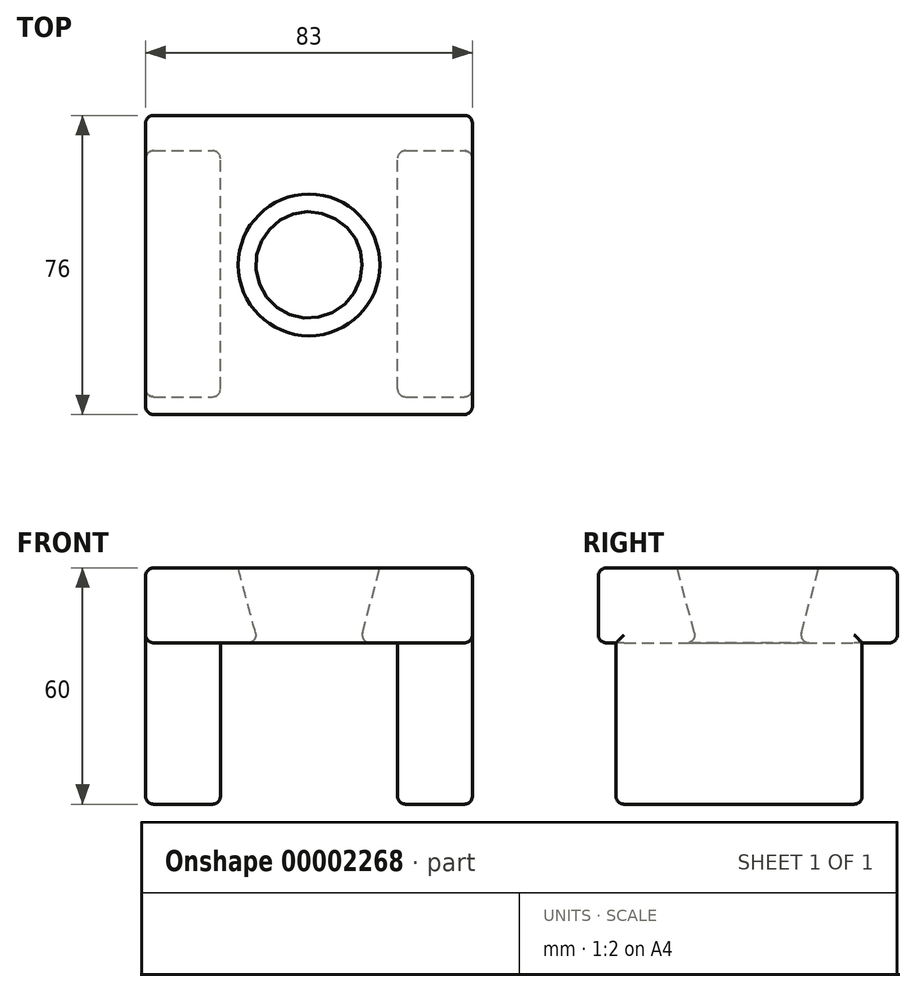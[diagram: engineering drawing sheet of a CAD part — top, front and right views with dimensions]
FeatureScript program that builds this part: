
annotation { "Feature Type Name" : "Feature", "Feature Type Description" : "" }
export const myFeature = defineFeature(function(context is Context, id is Id, definition is map)
    precondition{}
    {
        {
            var Q0;
            Q0=qCreatedBy(makeId("Top.planeOp"),FACE);
            var sketch = newSketch(context, id + "F0", { "sketchPlane" : qUnion([Q0])});
            skCircle(sketch, "E0", {"center": v(0, 0) * mm, "radius": 18 * mm});
            skLineSegment(sketch, "E1.bottom", {"start": v(41.5, 38) * mm, "end": v(-41.5, 38) * mm});
            skLineSegment(sketch, "E1.top", {"start": v(41.5, -38) * mm, "end": v(-41.5, -38) * mm});
            skLineSegment(sketch, "E1.left", {"start": v(41.5, 38) * mm, "end": v(41.5, -38) * mm});
            skLineSegment(sketch, "E1.right", {"start": v(-41.5, 38) * mm, "end": v(-41.5, -38) * mm});
            skSolve(sketch);
        }
        {
            var Q0;
            Q0=makeQuery(id+"F0.imprint","IMPRINT",FACE,{"disambiguationData":[TD([[makeQuery(id+"F0.imprint","IMPRINT",EDGE,{"derivedFrom":sQuery(id+"F0.wireOp",EDGE,"E0")}),-1.0]])]});
            var Q1;
            Q1=makeQuery(id+"F0.imprint","IMPRINT",FACE,{"disambiguationData":[TD([[makeQuery(id+"F0.imprint","IMPRINT",EDGE,{"derivedFrom":sQuery(id+"F0.wireOp",EDGE,"E0")}),1.0]])]});
            extrude(context, id + "F1", {"entities" : qUnion([Q0, Q1]), "oppositeDirection" : true, "depth" : 19 * mm, "offsetDistance" : 25 * mm});
        }
        {
            var Q0;
            Q0=makeQuery(id+"F0.imprint","IMPRINT",FACE,{"disambiguationData":[TD([[makeQuery(id+"F0.imprint","IMPRINT",EDGE,{"derivedFrom":sQuery(id+"F0.wireOp",EDGE,"E0")}),1.0]])]});
            extrude(context, id + "F2", {"entities" : qUnion([Q0]), "operationType" : NewBodyOperationType.REMOVE, "oppositeDirection" : true, "depth" : 25 * mm, "offsetDistance" : 25 * mm, "hasDraft" : true, "draftAngle" : 15 * degree, "draftPullDirection" : true});
        }
        {
            var Q0;
            Q0=makeQuery(id+"F1.opExtrude","CAP_FACE",FACE,{"disambiguationData":[OSD([sQuery(id+"F0.wireOp",EDGE,"E1.bottom"),sQuery(id+"F0.wireOp",EDGE,"E1.top"),sQuery(id+"F0.wireOp",EDGE,"E1.left"),sQuery(id+"F0.wireOp",EDGE,"E1.right")])],"isStart":false});
            var sketch = newSketch(context, id + "F3", { "sketchPlane" : qUnion([Q0])});
            skLineSegment(sketch, "E2.bottom", {"start": v(-41.5, 38) * mm, "end": v(-22.5, 38) * mm});
            skLineSegment(sketch, "E2.top", {"start": v(-41.5, -38) * mm, "end": v(-22.5, -38) * mm});
            skLineSegment(sketch, "E2.left", {"start": v(-41.5, 38) * mm, "end": v(-41.5, -38) * mm});
            skLineSegment(sketch, "E2.right", {"start": v(-22.5, 38) * mm, "end": v(-22.5, -38) * mm});
            skLineSegment(sketch, "E3.bottom", {"start": v(41.5, 38) * mm, "end": v(22.5, 38) * mm});
            skLineSegment(sketch, "E3.top", {"start": v(41.5, -38) * mm, "end": v(22.5, -38) * mm});
            skLineSegment(sketch, "E3.left", {"start": v(41.5, 38) * mm, "end": v(41.5, -38) * mm});
            skLineSegment(sketch, "E3.right", {"start": v(22.5, 38) * mm, "end": v(22.5, -38) * mm});
            skLineSegment(sketch, "E4", {"start": v(-41.5, 33.5) * mm, "end": v(41.5, 33.5) * mm});
            skLineSegment(sketch, "E5", {"start": v(-41.5, -29) * mm, "end": v(41.5, -29) * mm});
            skSolve(sketch);
        }
        {
            var Q0;
            {var subQ0=sQuery(id+"F3.wireOp",EDGE,"E4");var subQ1=sQuery(id+"F3.wireOp",EDGE,"E2.left");var subQ2=makeQuery(id+"F3.imprint","INTERSECT",VERTEX,{"derivedFrom":[subQ1,subQ0]});Q0=makeQuery(id+"F3.imprint","IMPRINT",FACE,{"disambiguationData":[TD([[makeQuery(id+"F3.imprint","IMPRINT",EDGE,{"disambiguationData":[TD([[subQ2,1.0]])],"derivedFrom":subQ1}),-1.0]])]});}
            var Q1;
            {var subQ0=sQuery(id+"F3.wireOp",EDGE,"E4");var subQ1=sQuery(id+"F3.wireOp",EDGE,"E3.left");var subQ2=makeQuery(id+"F3.imprint","INTERSECT",VERTEX,{"derivedFrom":[subQ1,subQ0]});Q1=makeQuery(id+"F3.imprint","IMPRINT",FACE,{"disambiguationData":[TD([[makeQuery(id+"F3.imprint","IMPRINT",EDGE,{"disambiguationData":[TD([[subQ2,1.0]])],"derivedFrom":subQ1}),1.0]])]});}
            extrude(context, id + "F4", {"entities" : qUnion([Q0, Q1]), "operationType" : NewBodyOperationType.ADD, "depth" : 41 * mm, "offsetDistance" : 25 * mm});
        }
        {
            var Q0;
            Q0=makeQuery(id+"F4.opExtrude","SWEPT_EDGE",EDGE,{"disambiguationData":[OSD([sQuery(id+"F3.wireOp",EDGE,"E2.left"),sQuery(id+"F3.wireOp",EDGE,"E4")])]});
            var Q1;
            Q1=makeQuery(id+"F4.opExtrude","CAP_EDGE",EDGE,{"disambiguationData":[OSD([sQuery(id+"F3.wireOp",EDGE,"E2.left")])],"isStart":false});
            var Q2;
            Q2=makeQuery(id+"F4.opExtrude","SWEPT_EDGE",EDGE,{"disambiguationData":[OSD([sQuery(id+"F3.wireOp",EDGE,"E2.left"),sQuery(id+"F3.wireOp",EDGE,"E5")])]});
            var Q3;
            Q3=makeQuery(id+"F4.opExtrude","SWEPT_EDGE",EDGE,{"disambiguationData":[OSD([sQuery(id+"F3.wireOp",EDGE,"E3.right"),sQuery(id+"F3.wireOp",EDGE,"E4")])]});
            var Q4;
            Q4=makeQuery(id+"F4.opExtrude","SWEPT_EDGE",EDGE,{"disambiguationData":[OSD([sQuery(id+"F3.wireOp",EDGE,"E2.right"),sQuery(id+"F3.wireOp",EDGE,"E4")])]});
            var Q5;
            Q5=makeQuery(id+"F4.opExtrude","CAP_EDGE",EDGE,{"disambiguationData":[OSD([sQuery(id+"F3.wireOp",EDGE,"E2.right")])],"isStart":false});
            var Q6;
            Q6=makeQuery(id+"F4.opExtrude","CAP_EDGE",EDGE,{"disambiguationData":[OSD([sQuery(id+"F3.wireOp",EDGE,"E3.right")])],"isStart":false});
            var Q7;
            {var subQ0=sQuery(id+"F3.wireOp",EDGE,"E5");Q7=makeQuery(id+"F4.opExtrude","CAP_EDGE",EDGE,{"disambiguationData":[OSD([subQ0]),TDD([makeQuery(id+"F3.imprint","IMPRINT",EDGE,{"disambiguationData":[TD([[makeQuery(id+"F3.imprint","INTERSECT",VERTEX,{"derivedFrom":[sQuery(id+"F3.wireOp",EDGE,"E3.left"),subQ0]}),1.0]])],"derivedFrom":subQ0})])],"isStart":false});}
            var Q8;
            {var subQ0=sQuery(id+"F3.wireOp",EDGE,"E5");Q8=makeQuery(id+"F4.opExtrude","CAP_EDGE",EDGE,{"disambiguationData":[OSD([subQ0]),TDD([makeQuery(id+"F3.imprint","IMPRINT",EDGE,{"disambiguationData":[TD([[makeQuery(id+"F3.imprint","INTERSECT",VERTEX,{"derivedFrom":[sQuery(id+"F3.wireOp",EDGE,"E2.left"),subQ0]}),-1.0]])],"derivedFrom":subQ0})])],"isStart":false});}
            var Q9;
            {var subQ0=sQuery(id+"F3.wireOp",EDGE,"E4");Q9=makeQuery(id+"F4.opExtrude","CAP_EDGE",EDGE,{"disambiguationData":[OSD([subQ0]),TDD([makeQuery(id+"F3.imprint","IMPRINT",EDGE,{"disambiguationData":[TD([[makeQuery(id+"F3.imprint","INTERSECT",VERTEX,{"derivedFrom":[sQuery(id+"F3.wireOp",EDGE,"E2.left"),subQ0]}),-1.0]])],"derivedFrom":subQ0})])],"isStart":false});}
            var Q10;
            Q10=makeQuery(id+"F4.opExtrude","SWEPT_EDGE",EDGE,{"disambiguationData":[OSD([sQuery(id+"F3.wireOp",EDGE,"E2.right"),sQuery(id+"F3.wireOp",EDGE,"E5")])]});
            var Q11;
            Q11=makeQuery(id+"F4.opExtrude","SWEPT_EDGE",EDGE,{"disambiguationData":[OSD([sQuery(id+"F3.wireOp",EDGE,"E3.right"),sQuery(id+"F3.wireOp",EDGE,"E5")])]});
            var Q12;
            Q12=makeQuery(id+"F4.opExtrude","SWEPT_EDGE",EDGE,{"disambiguationData":[OSD([sQuery(id+"F3.wireOp",EDGE,"E3.left"),sQuery(id+"F3.wireOp",EDGE,"E5")])]});
            var Q13;
            Q13=makeQuery(id+"F4.opExtrude","CAP_EDGE",EDGE,{"disambiguationData":[OSD([sQuery(id+"F3.wireOp",EDGE,"E3.left")])],"isStart":false});
            var Q14;
            {var subQ0=sQuery(id+"F3.wireOp",EDGE,"E4");Q14=makeQuery(id+"F4.opExtrude","CAP_EDGE",EDGE,{"disambiguationData":[OSD([subQ0]),TDD([makeQuery(id+"F3.imprint","IMPRINT",EDGE,{"disambiguationData":[TD([[makeQuery(id+"F3.imprint","INTERSECT",VERTEX,{"derivedFrom":[sQuery(id+"F3.wireOp",EDGE,"E3.left"),subQ0]}),1.0]])],"derivedFrom":subQ0})])],"isStart":false});}
            var Q15;
            Q15=makeQuery(id+"F4.opExtrude","SWEPT_EDGE",EDGE,{"disambiguationData":[OSD([sQuery(id+"F3.wireOp",EDGE,"E3.left"),sQuery(id+"F3.wireOp",EDGE,"E4")])]});
            var Q16;
            Q16=makeQuery(id+"F1.opExtrude","CAP_EDGE",EDGE,{"disambiguationData":[OSD([sQuery(id+"F0.wireOp",EDGE,"E1.left")])],"isStart":true});
            var Q17;
            Q17=makeQuery(id+"F1.opExtrude","SWEPT_EDGE",EDGE,{"disambiguationData":[OSD([sQuery(id+"F0.wireOp",EDGE,"E1.top"),sQuery(id+"F0.wireOp",EDGE,"E1.left")])]});
            var Q18;
            Q18=makeQuery(id+"F1.opExtrude","CAP_EDGE",EDGE,{"disambiguationData":[OSD([sQuery(id+"F0.wireOp",EDGE,"E1.top")])],"isStart":true});
            var Q19;
            Q19=makeQuery(id+"F1.opExtrude","SWEPT_EDGE",EDGE,{"disambiguationData":[OSD([sQuery(id+"F0.wireOp",EDGE,"E1.top"),sQuery(id+"F0.wireOp",EDGE,"E1.right")])]});
            var Q20;
            Q20=makeQuery(id+"F1.opExtrude","CAP_EDGE",EDGE,{"disambiguationData":[OSD([sQuery(id+"F0.wireOp",EDGE,"E1.right")])],"isStart":true});
            var Q21;
            Q21=makeQuery(id+"F1.opExtrude","CAP_EDGE",EDGE,{"disambiguationData":[OSD([sQuery(id+"F0.wireOp",EDGE,"E1.top")])],"isStart":false});
            var Q22;
            Q22=makeQuery(id+"F1.opExtrude","CAP_EDGE",EDGE,{"disambiguationData":[OSD([sQuery(id+"F0.wireOp",EDGE,"E1.bottom")])],"isStart":true});
            var Q23;
            Q23=makeQuery(id+"F1.opExtrude","CAP_EDGE",EDGE,{"disambiguationData":[OSD([sQuery(id+"F0.wireOp",EDGE,"E1.bottom")])],"isStart":false});
            var Q24;
            Q24=makeQuery(id+"F1.opExtrude","SWEPT_EDGE",EDGE,{"disambiguationData":[OSD([sQuery(id+"F0.wireOp",EDGE,"E1.bottom"),sQuery(id+"F0.wireOp",EDGE,"E1.right")])]});
            var Q25;
            Q25=makeQuery(id+"F1.opExtrude","SWEPT_EDGE",EDGE,{"disambiguationData":[OSD([sQuery(id+"F0.wireOp",EDGE,"E1.bottom"),sQuery(id+"F0.wireOp",EDGE,"E1.left")])]});
            var Q26;
            Q26=makeQuery(id+"F2.boolean.opBoolean","COPY",EDGE,{"derivedFrom":makeQuery(id+"F2.opExtrude","CAP_EDGE",EDGE,{"disambiguationData":[OSD([sQuery(id+"F0.wireOp",EDGE,"E0")])],"isStart":true})});
            var Q27;
            Q27=makeQuery(id+"F2.boolean.opBoolean","INTERSECT",EDGE,{"derivedFrom":[makeQuery(id+"F1.opExtrude","CAP_FACE",FACE,{"disambiguationData":[OSD([sQuery(id+"F0.wireOp",EDGE,"E1.bottom"),sQuery(id+"F0.wireOp",EDGE,"E1.top"),sQuery(id+"F0.wireOp",EDGE,"E1.left"),sQuery(id+"F0.wireOp",EDGE,"E1.right")])],"isStart":false}),makeQuery(id+"F2.opExtrude","SWEPT_FACE",FACE,{"disambiguationData":[OSD([sQuery(id+"F0.wireOp",EDGE,"E0")])]})]});
            var Q28;
            {var subQ0=sQuery(id+"F0.wireOp",EDGE,"E1.right");var subQ2=sQuery(id+"F0.wireOp",EDGE,"E1.top");Q28=makeQuery(id+"F4.boolean.opBoolean","SPLIT",EDGE,{"disambiguationData":[TD([makeQuery(id+"F1.opExtrude","SWEPT_FACE",FACE,{"disambiguationData":[OSD([subQ2])]})])],"derivedFrom":makeQuery(id+"F1.opExtrude","CAP_EDGE",EDGE,{"disambiguationData":[OSD([subQ0])],"isStart":false})});}
            var Q29;
            {var subQ0=sQuery(id+"F0.wireOp",EDGE,"E1.left");var subQ1=sQuery(id+"F0.wireOp",EDGE,"E1.top");Q29=makeQuery(id+"F4.boolean.opBoolean","SPLIT",EDGE,{"disambiguationData":[TD([makeQuery(id+"F1.opExtrude","SWEPT_FACE",FACE,{"disambiguationData":[OSD([subQ1])]})])],"derivedFrom":makeQuery(id+"F1.opExtrude","CAP_EDGE",EDGE,{"disambiguationData":[OSD([subQ0])],"isStart":false})});}
            var Q30;
            {var subQ1=sQuery(id+"F0.wireOp",EDGE,"E1.right");var subQ2=sQuery(id+"F0.wireOp",EDGE,"E1.bottom");Q30=makeQuery(id+"F4.boolean.opBoolean","SPLIT",EDGE,{"disambiguationData":[TD([makeQuery(id+"F1.opExtrude","SWEPT_FACE",FACE,{"disambiguationData":[OSD([subQ2])]})])],"derivedFrom":makeQuery(id+"F1.opExtrude","CAP_EDGE",EDGE,{"disambiguationData":[OSD([subQ1])],"isStart":false})});}
            var Q31;
            {var subQ0=sQuery(id+"F0.wireOp",EDGE,"E1.left");var subQ2=sQuery(id+"F0.wireOp",EDGE,"E1.bottom");Q31=makeQuery(id+"F4.boolean.opBoolean","SPLIT",EDGE,{"disambiguationData":[TD([makeQuery(id+"F1.opExtrude","SWEPT_FACE",FACE,{"disambiguationData":[OSD([subQ2])]})])],"derivedFrom":makeQuery(id+"F1.opExtrude","CAP_EDGE",EDGE,{"disambiguationData":[OSD([subQ0])],"isStart":false})});}
            fillet(context, id + "F5", {"entities" : qUnion([Q0, Q1, Q2, Q3, Q4, Q5, Q6, Q7, Q8, Q9, Q10, Q11, Q12, Q13, Q14, Q15, Q16, Q17, Q18, Q19, Q20, Q21, Q22, Q23, Q24, Q25, Q26, Q27, Q28, Q29, Q30, Q31]), "tangentPropagation" : true, "radius" : 2 * mm, "defaultsChanged" : false, "vertexSettings" : [], "allowEdgeOverflow" : false});
        }
    });
